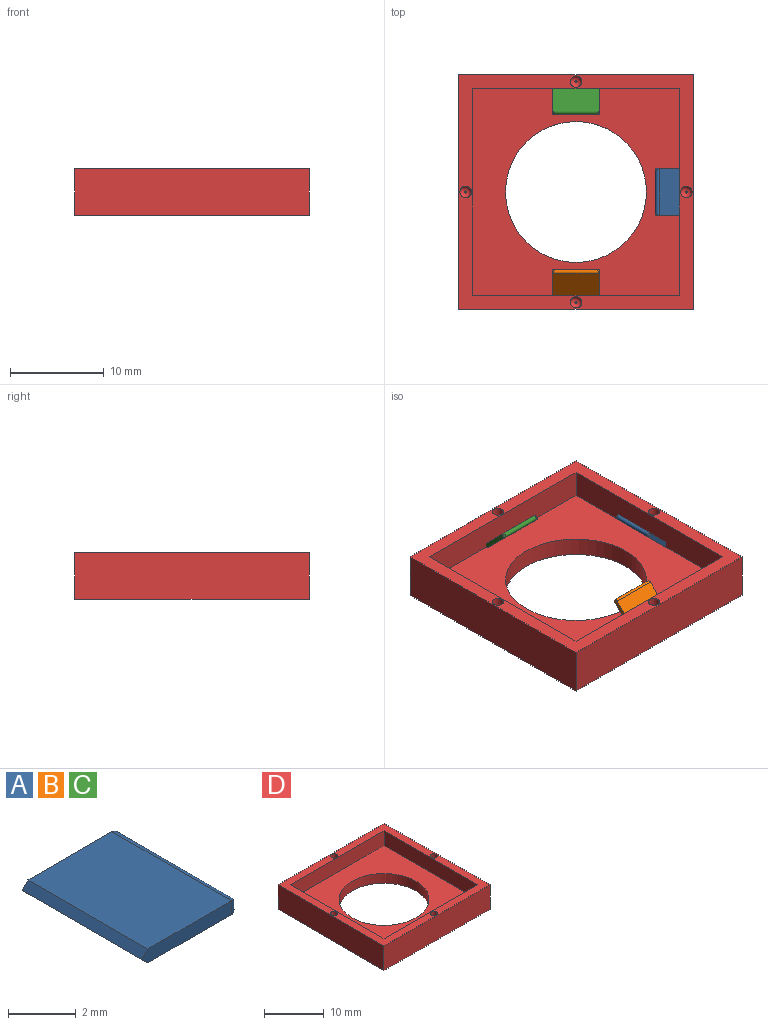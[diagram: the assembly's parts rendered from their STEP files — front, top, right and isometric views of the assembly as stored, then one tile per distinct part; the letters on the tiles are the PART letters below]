
ASSEMBLY  parts=4 mates=3
PART A: 9 faces, bbox 4x5x0.5 mm
  f0: plane 3.75x0.5mm, normal (0,-1,0), area 1.8mm2, adj f1,f3,f6,f7,f8
  f1: plane 5x3.5mm, normal (0,0,-1), area 17.5mm2, adj f0,f2,f5,f8
  f2: plane 3.75x0.5mm, normal (0,1,0), area 1.8mm2, adj f1,f3,f4,f7,f8
  f3: plane 5x3.5mm, normal (0,0,1), area 17.5mm2, adj f0,f2,f5,f7
  f4: cylinder r=0.25mm len=0.5mm, axis (0,0,1), area 0.1mm2, adj f2,f5
  f5: cylinder r=0.25mm len=5mm, axis (0,-1,0), area 3.7mm2, adj f1,f3,f4,f6
  f6: cylinder r=0.25mm len=0.5mm, axis (0,0,-1), area 0.1mm2, adj f0,f5
  f7: plane 5x0.25mm, normal (-0.71,0,0.71), area 1.8mm2, adj f0,f2,f3,f8
  f8: plane 5x0.25mm, normal (-0.71,0,-0.71), area 1.8mm2, adj f0,f1,f2,f7
PART B: same geometry as A
PART C: same geometry as A
PART D: 24 faces, bbox 25x25x5 mm
  f0: plane 25x25mm, normal (0,0,1), area 136.3mm2, adj f2,f3,f4,f5,f7,f8,f9,f10
  f1: cylinder r=7.5mm len=15mm, axis (0,0,1), area 94.2mm2, adj f6,f11
  f2: plane 25x5mm, normal (0,-1,0), area 125mm2, adj f0,f3,f5,f6
  f3: plane 25x5mm, normal (1,0,0), area 125mm2, adj f0,f2,f4,f6
  f4: plane 25x5mm, normal (0,1,0), area 125mm2, adj f0,f3,f5,f6
  f5: plane 25x5mm, normal (-1,0,0), area 125mm2, adj f0,f2,f4,f6
  f6: plane 25x25mm, normal (0,0,-1), area 448.3mm2, adj f1,f2,f3,f4,f5
  f7: plane 22x3mm, normal (0,1,0), area 66mm2, adj f0,f8,f10,f11
  f8: plane 22x3mm, normal (-1,0,0), area 66mm2, adj f0,f7,f9,f11
  f9: plane 22x3mm, normal (0,-1,0), area 66mm2, adj f0,f8,f10,f11
  f10: plane 22x3mm, normal (1,0,0), area 66mm2, adj f0,f7,f9,f11
  f11: plane 22x22mm, normal (0,0,1), area 307.3mm2, adj f1,f7,f8,f9,f10
  f12: cylinder r=0.61mm len=1.5mm, axis (0,0,1), area 5.7mm2, adj f0,f20
  f13: plane 0.22x0.22mm, normal (0,0,1), area 0mm2, adj f20
  f14: cylinder r=0.61mm len=1.5mm, axis (0,0,1), area 5.7mm2, adj f0,f21
  f15: plane 0.22x0.22mm, normal (0,0,1), area 0mm2, adj f21
  f16: cylinder r=0.61mm len=1.5mm, axis (0,0,1), area 5.7mm2, adj f0,f22
  f17: plane 0.22x0.22mm, normal (0,0,1), area 0mm2, adj f22
  f18: cylinder r=0.61mm len=1.5mm, axis (0,0,1), area 5.7mm2, adj f0,f23
  f19: plane 0.22x0.22mm, normal (0,0,1), area 0mm2, adj f23
  f20: torus R=0.11mm, axis (0,0,1), area 2.1mm2, adj f12,f13
  f21: torus R=0.11mm, axis (0,0,1), area 2.1mm2, adj f14,f15
  f22: torus R=0.11mm, axis (0,0,1), area 2.1mm2, adj f16,f17
  f23: torus R=0.11mm, axis (0,0,1), area 2.1mm2, adj f18,f19
PLACE A rot(axis=(-0.38,0,-0.92),180deg) t=(6.14,-0.25,4.15)mm
PLACE B rot(axis=(0.36,-0.36,0.86),98.4deg) t=(-3.98,-10.19,4.15)mm
PLACE C rot(axis=(-0.36,-0.36,-0.86),98.4deg) t=(-3.98,9.68,4.15)mm
PLACE D t=(-3.98,-0.25,0.56)mm
MATE fastened A.f8 <-> D.f11  axis (0,0,-1) through (7.02,-0.25,2.56)mm
MATE fastened C.f8 <-> D.f11  axis (0,0,-1) through (-3.98,10.75,2.56)mm
MATE fastened B.f8 <-> D.f11  axis (0,0,-1) through (-3.98,-11.25,2.56)mm
